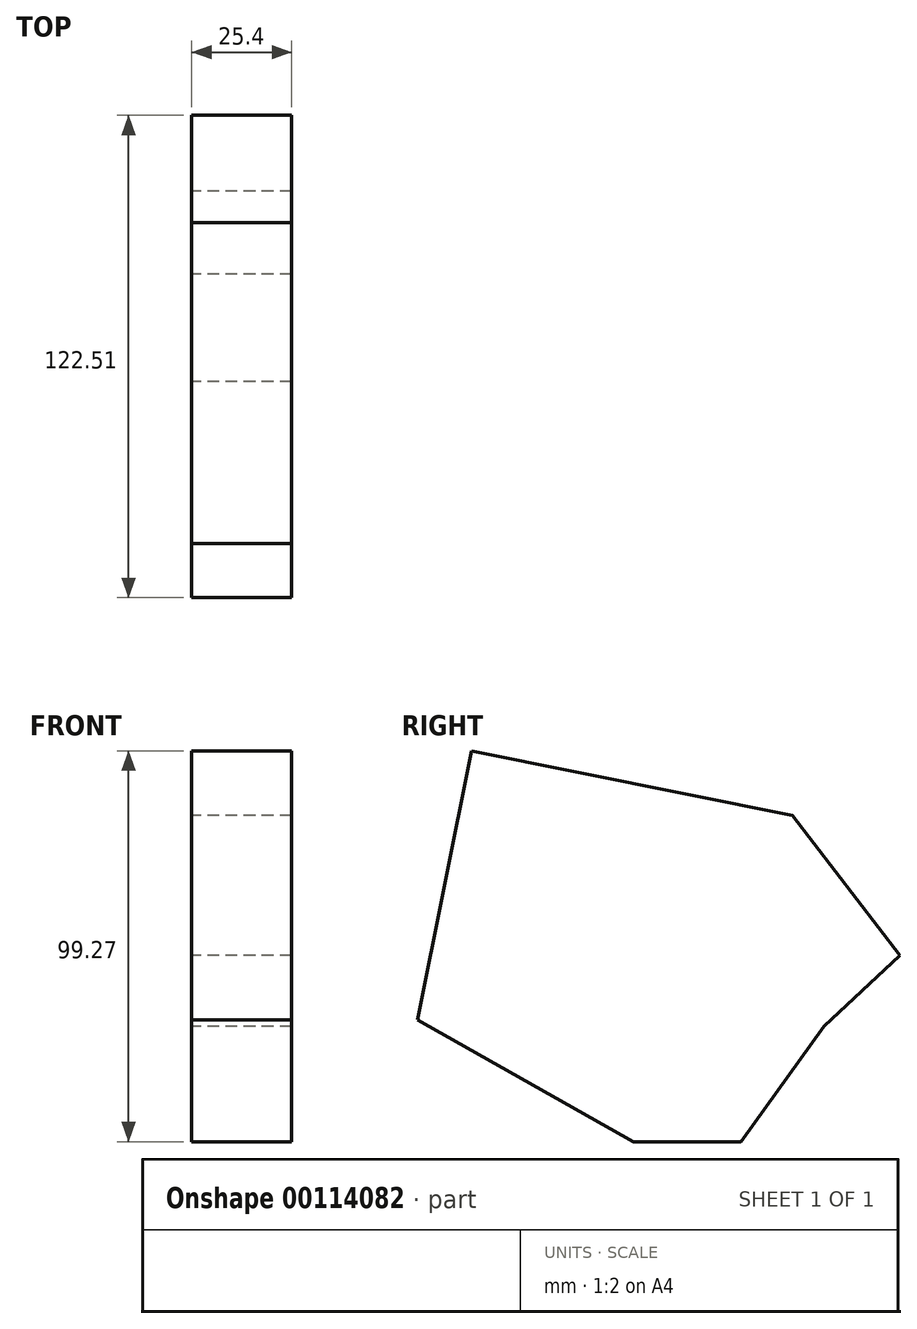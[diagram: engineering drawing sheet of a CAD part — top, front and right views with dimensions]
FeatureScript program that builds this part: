
annotation { "Feature Type Name" : "Feature", "Feature Type Description" : "" }
export const myFeature = defineFeature(function(context is Context, id is Id, definition is map)
    precondition{}
    {
        {
            var Q0;
            Q0=qCreatedBy(makeId("Right.planeOp"),FACE);
            var sketch = newSketch(context, id + "F0", { "sketchPlane" : qUnion([Q0])});
            skLineSegment(sketch, "E0", {"start": v(-8.6, 9.59) * mm, "end": v(31.8, 35.53) * mm});
            skLineSegment(sketch, "E1", {"start": v(31.8, 35.53) * mm, "end": v(59.02, 0) * mm});
            skLineSegment(sketch, "E2", {"start": v(-8.6, 9.59) * mm, "end": v(39.7, -18.11) * mm});
            skLineSegment(sketch, "E3", {"start": v(59.02, 0) * mm, "end": v(39.7, -18.11) * mm});
            skArc(sketch, "E4", {"start": v(-49.75, 51.92) * mm, "mid": v(-55.55, 5.12) * mm, "end": v(-8.6, 9.59) * mm});
            skLineSegment(sketch, "E5", {"start": v(-49.75, 51.92) * mm, "end": v(31.8, 35.53) * mm});
            skLineSegment(sketch, "E6.bottom", {"start": v(-8.6, 9.59) * mm, "end": v(18.67, 9.59) * mm});
            skLineSegment(sketch, "E6.top", {"start": v(-8.6, -47.35) * mm, "end": v(18.67, -47.35) * mm});
            skLineSegment(sketch, "E6.left", {"start": v(-8.6, 9.59) * mm, "end": v(-8.6, -47.35) * mm});
            skLineSegment(sketch, "E6.right", {"start": v(18.67, 9.59) * mm, "end": v(18.67, -47.35) * mm});
            skLineSegment(sketch, "E7", {"start": v(39.7, -18.11) * mm, "end": v(18.67, -47.35) * mm});
            skLineSegment(sketch, "E8", {"start": v(-8.6, -47.35) * mm, "end": v(-33.87, 26.2) * mm});
            skLineSegment(sketch, "E9", {"start": v(-49.75, 51.92) * mm, "end": v(-63.5, -16.45) * mm});
            skLineSegment(sketch, "E10", {"start": v(-63.5, -16.45) * mm, "end": v(-8.6, -47.35) * mm});
            skSolve(sketch);
        }
        {
            var Q0;
            {var subQ2=sQuery(id+"F0.wireOp",EDGE,"E0");Q0=makeQuery(id+"F0.imprint","IMPRINT",FACE,{"disambiguationData":[TD([[makeQuery(id+"F0.imprint","IMPRINT",EDGE,{"derivedFrom":subQ2}),1.0]])]});}
            var Q1;
            {var subQ5=sQuery(id+"F0.wireOp",EDGE,"E10");Q1=makeQuery(id+"F0.imprint","IMPRINT",FACE,{"disambiguationData":[TD([[makeQuery(id+"F0.imprint","IMPRINT",EDGE,{"derivedFrom":subQ5}),1.0]])]});}
            var Q2;
            {var subQ0=sQuery(id+"F0.wireOp",EDGE,"E6.left");Q2=makeQuery(id+"F0.imprint","IMPRINT",FACE,{"disambiguationData":[TD([[makeQuery(id+"F0.imprint","IMPRINT",EDGE,{"derivedFrom":subQ0}),-1.0]])]});}
            var Q3;
            {var subQ4=sQuery(id+"F0.wireOp",EDGE,"E6.top");Q3=makeQuery(id+"F0.imprint","IMPRINT",FACE,{"disambiguationData":[TD([[makeQuery(id+"F0.imprint","IMPRINT",EDGE,{"derivedFrom":subQ4}),1.0]])]});}
            var Q4;
            {var subQ0=sQuery(id+"F0.wireOp",EDGE,"E7");Q4=makeQuery(id+"F0.imprint","IMPRINT",FACE,{"disambiguationData":[TD([[makeQuery(id+"F0.imprint","IMPRINT",EDGE,{"derivedFrom":subQ0}),-1.0]])]});}
            var Q5;
            {var subQ0=sQuery(id+"F0.wireOp",EDGE,"E6.bottom");Q5=makeQuery(id+"F0.imprint","IMPRINT",FACE,{"disambiguationData":[TD([[makeQuery(id+"F0.imprint","IMPRINT",EDGE,{"derivedFrom":subQ0}),-1.0]])]});}
            var Q6;
            Q6=makeQuery(id+"F0.imprint","IMPRINT",FACE,{"disambiguationData":[TD([[makeQuery(id+"F0.imprint","IMPRINT",EDGE,{"derivedFrom":sQuery(id+"F0.wireOp",EDGE,"E0")}),-1.0]])]});
            extrude(context, id + "F1", {"entities" : qUnion([Q0, Q1, Q2, Q3, Q4, Q5, Q6]), "depth" : 25.4 * mm});
        }
    });
